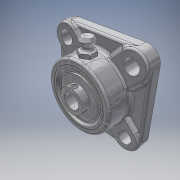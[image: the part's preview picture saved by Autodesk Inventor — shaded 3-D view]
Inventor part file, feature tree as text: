
AUTODESK INVENTOR PART (.ipt)
format: ipt  version: 2019 (Build 230136000, 136)  size: 728,576 bytes
history: native  units: in
note: dims shown in document units (in); Inventor stores cm internally (conversion verified against a paired STEP export)
features: other x2, pattern_circular x2, chamfer x1
ambient origin geometry x8: Origin, YZ Plane, XZ Plane, XY Plane, X Axis, Y Axis, Z Axis, Center Point
bodies: Solid1 (feature_tree), Solid2 (feature_tree), Solid3 (feature_tree), Solid4 (feature_tree), Solid5 (feature_tree)
feature tree (5):
  chamfer  "Chamfer3"  [1 undecoded]
  other  "Cut-Extrude3"
  pattern_circular  "CirPattern1"
  pattern_circular  "CirPattern2"
  other  "Cut-Extrude4"
note: 1 required parameter value undecoded (feature->parameter linkage not recoverable at this tier; creation-order binding heuristic only, values carry confidence <= 0.55)
